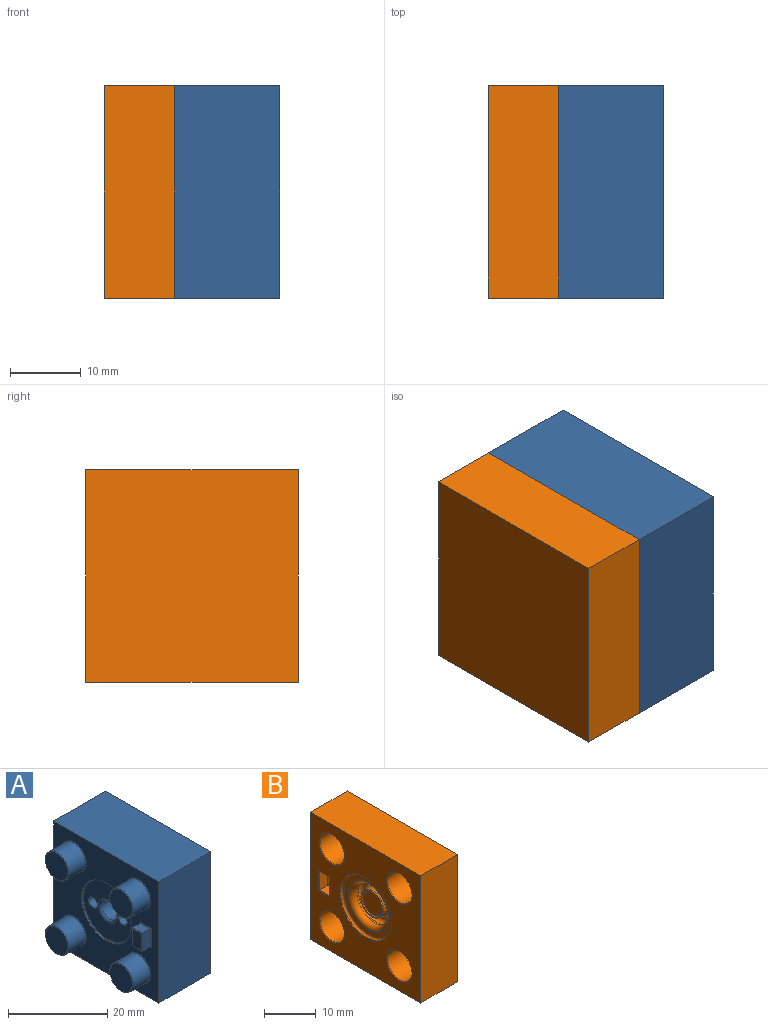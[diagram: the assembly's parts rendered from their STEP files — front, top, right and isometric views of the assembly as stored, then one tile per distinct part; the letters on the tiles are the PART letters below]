
ASSEMBLY  parts=2 mates=1
PART A: 49 faces, bbox 20.1x30.2x30.2 mm
  f0: plane 13.91x13.91mm, normal (-1,0,0), area 118.4mm2, adj f9,f10,f47,f48
  f1: plane 30x14.83mm, normal (0,0,-1), area 444.9mm2, adj f3,f4,f5,f6
  f2: plane 30x14.83mm, normal (0,0,1), area 444.9mm2, adj f3,f4,f5,f6
  f3: plane 30.01x30.01mm, normal (1,0,0), area 888.6mm2, adj f1,f2,f4,f5,f25,f47,f48
  f4: plane 30x14.83mm, normal (0,-1,0), area 444.9mm2, adj f1,f2,f3,f6
  f5: plane 30x14.83mm, normal (0,1,0), area 444.9mm2, adj f1,f2,f3,f6
  f6: plane 30x30mm, normal (-1,0,0), area 573.2mm2, adj f1,f2,f4,f5,f11,f31,f32,f36
  f7: plane 4.65x4.65mm, normal (-1,0,0), area 13.5mm2, adj f8,f27,f28,f29,f30
  f8: cylinder r=2.25mm len=11.5mm, axis (-1,0,0), area 162.6mm2, adj f7,f9
  f9: torus R=2.75mm, axis (1,0,0), area 12mm2, adj f0,f8
  f10: torus R=6.96mm, axis (-1,0,0), area 10.4mm2, adj f0,f11
  f11: cylinder r=7.11mm len=14.21mm, axis (-1,0,0), area 13.4mm2, adj f6,f10
  f12: cylinder r=3.35mm len=6.69mm, axis (1,0,0), area 98.8mm2, adj f32,f33
  f13: plane 6.39x6.39mm, normal (-1,0,0), area 32.1mm2, adj f33
  f14: cylinder r=3.35mm len=6.69mm, axis (1,0,0), area 98.8mm2, adj f31,f34
  f15: plane 6.39x6.39mm, normal (-1,0,0), area 32.1mm2, adj f34
  f16: cylinder r=3.35mm len=6.69mm, axis (1,0,0), area 98.8mm2, adj f35,f46
  f17: plane 6.39x6.39mm, normal (-1,0,0), area 32.1mm2, adj f35
  f18: cylinder r=3.35mm len=6.69mm, axis (1,0,0), area 98.8mm2, adj f36,f37
  f19: plane 6.39x6.39mm, normal (-1,0,0), area 32.1mm2, adj f37
  f20: plane 2.75x2.2mm, normal (0,0,1), area 6.1mm2, adj f21,f23,f38,f43
  f21: plane 4.5x2.2mm, normal (0,1,0), area 9.9mm2, adj f20,f22,f39,f42
  f22: plane 2.75x2.2mm, normal (0,0,-1), area 6.1mm2, adj f21,f23,f41,f44
  f23: plane 4.5x2.2mm, normal (0,-1,0), area 9.9mm2, adj f20,f22,f40,f45
  f24: plane 4.2x2.45mm, normal (-1,0,0), area 10.3mm2, adj f42,f43,f44,f45
  f25: cone r=1mm half-angle=45deg, axis (-1,0,0), area 1mm2, adj f3,f26,f27,f28,f30
  f26: cone r=1mm half-angle=45deg, axis (-1,0,0), area 0.2mm2, adj f25,f28,f29,f30
  f27: cylinder r=0.74mm len=2.34mm, axis (-1,0,0), area 1.3mm2, adj f7,f25,f28,f30
  f28: bspline ~2.55x2.31mm, area 9.1mm2, adj f7,f25,f26,f27,f29
  f29: cylinder r=1mm len=2.08mm, axis (1,0,0), area 1.6mm2, adj f7,f26,f28,f30
  f30: bspline ~2.68x2.31mm, area 9.1mm2, adj f7,f25,f26,f27,f29
  f31: torus R=3.5mm, axis (-1,0,0), area 5mm2, adj f6,f14
  f32: torus R=3.5mm, axis (-1,0,0), area 5mm2, adj f6,f12
  f33: torus R=3.2mm, axis (-1,0,0), area 4.9mm2, adj f12,f13
  f34: torus R=3.2mm, axis (-1,0,0), area 4.9mm2, adj f14,f15
  f35: torus R=3.2mm, axis (-1,0,0), area 4.9mm2, adj f16,f17
  f36: torus R=3.5mm, axis (-1,0,0), area 5mm2, adj f6,f18
  f37: torus R=3.2mm, axis (-1,0,0), area 4.9mm2, adj f18,f19
  f38: cylinder r=0.15mm len=3.05mm, axis (0,-1,0), area 0.7mm2, adj f6,f20,f39,f40
  f39: cylinder r=0.15mm len=4.8mm, axis (0,0,1), area 1.1mm2, adj f6,f21,f38,f41
  f40: cylinder r=0.15mm len=4.8mm, axis (0,0,-1), area 1.1mm2, adj f6,f23,f38,f41
  f41: cylinder r=0.15mm len=3.05mm, axis (0,1,0), area 0.7mm2, adj f6,f22,f39,f40
  f42: cylinder r=0.15mm len=4.5mm, axis (0,0,-1), area 1mm2, adj f21,f24,f43,f44
  f43: cylinder r=0.15mm len=2.75mm, axis (0,1,0), area 0.6mm2, adj f20,f24,f42,f45
  f44: cylinder r=0.15mm len=2.75mm, axis (0,-1,0), area 0.6mm2, adj f22,f24,f42,f45
  f45: cylinder r=0.15mm len=4.5mm, axis (0,0,1), area 1mm2, adj f23,f24,f43,f44
  f46: torus R=3.5mm, axis (-1,0,0), area 5mm2, adj f6,f16
  f47: cylinder r=1.25mm len=14.38mm, axis (-1,0,0), area 112.9mm2, adj f0,f3
  f48: cylinder r=1.25mm len=14.38mm, axis (-1,0,0), area 112.9mm2, adj f0,f3
PART B: 49 faces, bbox 10x30x30 mm
  f0: plane 30x10mm, normal (0,-1,0), area 300mm2, adj f1,f3,f4,f48
  f1: plane 30x10mm, normal (0,0,-1), area 300mm2, adj f0,f2,f3,f48
  f2: plane 30x10mm, normal (0,1,0), area 300mm2, adj f1,f3,f4,f48
  f3: plane 30x30mm, normal (-1,0,0), area 573.2mm2, adj f0,f1,f2,f4,f18,f32,f33,f37
  f4: plane 30x10mm, normal (0,0,1), area 300mm2, adj f0,f2,f3,f48
  f5: plane 5.19x5.19mm, normal (-1,0,0), area 21.2mm2, adj f6
  f6: torus R=2.6mm, axis (1,0,0), area 5.4mm2, adj f5,f7
  f7: cylinder r=2.8mm len=5.59mm, axis (1,0,0), area 0.9mm2, adj f6,f8
  f8: plane 6x6mm, normal (-1,0,0), area 3.7mm2, adj f7,f9
  f9: cylinder r=3mm len=6mm, axis (1,0,0), area 4.7mm2, adj f8,f10
  f10: cone r=3mm half-angle=20.8deg, axis (1,0,0), area 40.3mm2, adj f9,f11
  f11: torus R=4.2mm, axis (1,0,0), area 13.7mm2, adj f10,f12
  f12: torus R=4.24mm, axis (1,0,0), area 48mm2, adj f11,f13
  f13: cone r=5.04mm half-angle=6.3deg, axis (1,0,0), area 16.3mm2, adj f12,f14
  f14: torus R=5.55mm, axis (1,0,0), area 70.9mm2, adj f13,f15
  f15: revolved ~11.03x11.03mm, area 5mm2, adj f14,f16
  f16: plane 13.21x13.21mm, normal (-1,0,0), area 41.5mm2, adj f15,f17
  f17: torus R=6.61mm, axis (1,0,0), area 34.2mm2, adj f16,f18
  f18: cylinder r=7.11mm len=14.21mm, axis (1,0,0), area 10.5mm2, adj f3,f17
  f19: plane 4.2x2.45mm, normal (-1,0,0), area 10.3mm2, adj f43,f44,f45,f46
  f20: plane 4.5x2.2mm, normal (0,-1,0), area 9.9mm2, adj f21,f23,f41,f46
  f21: plane 2.75x2.2mm, normal (0,0,1), area 6.1mm2, adj f20,f22,f42,f45
  f22: plane 4.5x2.2mm, normal (0,1,0), area 9.9mm2, adj f21,f23,f40,f43
  f23: plane 2.75x2.2mm, normal (0,0,-1), area 6.1mm2, adj f20,f22,f39,f44
  f24: plane 6.39x6.39mm, normal (-1,0,0), area 32.1mm2, adj f38
  f25: cylinder r=3.35mm len=6.69mm, axis (-1,0,0), area 98.8mm2, adj f37,f38
  f26: plane 6.39x6.39mm, normal (-1,0,0), area 32.1mm2, adj f36
  f27: cylinder r=3.35mm len=6.69mm, axis (-1,0,0), area 98.8mm2, adj f36,f47
  f28: plane 6.39x6.39mm, normal (-1,0,0), area 32.1mm2, adj f35
  f29: cylinder r=3.35mm len=6.69mm, axis (-1,0,0), area 98.8mm2, adj f32,f35
  f30: cylinder r=3.35mm len=6.69mm, axis (-1,0,0), area 98.8mm2, adj f33,f34
  f31: plane 6.39x6.39mm, normal (-1,0,0), area 32.1mm2, adj f34
  f32: torus R=3.5mm, axis (1,0,0), area 5mm2, adj f3,f29
  f33: torus R=3.5mm, axis (1,0,0), area 5mm2, adj f3,f30
  f34: torus R=3.2mm, axis (1,0,0), area 4.9mm2, adj f30,f31
  f35: torus R=3.2mm, axis (1,0,0), area 4.9mm2, adj f28,f29
  f36: torus R=3.2mm, axis (1,0,0), area 4.9mm2, adj f26,f27
  f37: torus R=3.5mm, axis (1,0,0), area 5mm2, adj f3,f25
  f38: torus R=3.2mm, axis (1,0,0), area 4.9mm2, adj f24,f25
  f39: cylinder r=0.15mm len=3.05mm, axis (0,1,0), area 0.7mm2, adj f3,f23,f40,f41
  f40: cylinder r=0.15mm len=4.8mm, axis (0,0,1), area 1.1mm2, adj f3,f22,f39,f42
  f41: cylinder r=0.15mm len=4.8mm, axis (0,0,-1), area 1.1mm2, adj f3,f20,f39,f42
  f42: cylinder r=0.15mm len=3.05mm, axis (0,-1,0), area 0.7mm2, adj f3,f21,f40,f41
  f43: cylinder r=0.15mm len=4.5mm, axis (0,0,-1), area 1mm2, adj f19,f22,f44,f45
  f44: cylinder r=0.15mm len=2.75mm, axis (0,-1,0), area 0.6mm2, adj f19,f23,f43,f46
  f45: cylinder r=0.15mm len=2.75mm, axis (0,1,0), area 0.6mm2, adj f19,f21,f43,f46
  f46: cylinder r=0.15mm len=4.5mm, axis (0,0,1), area 1mm2, adj f19,f20,f44,f45
  f47: torus R=3.5mm, axis (1,0,0), area 5mm2, adj f3,f27
  f48: plane 30x30mm, normal (1,0,0), area 900mm2, adj f0,f1,f2,f4
PLACE A at identity
PLACE B rot(axis=(0,0,-1),180deg) t=(3.46,0,0)mm
MATE slider B.f19 <-> A.f24  axis (1,0,0) through (-0.77,-11.25,0)mm
